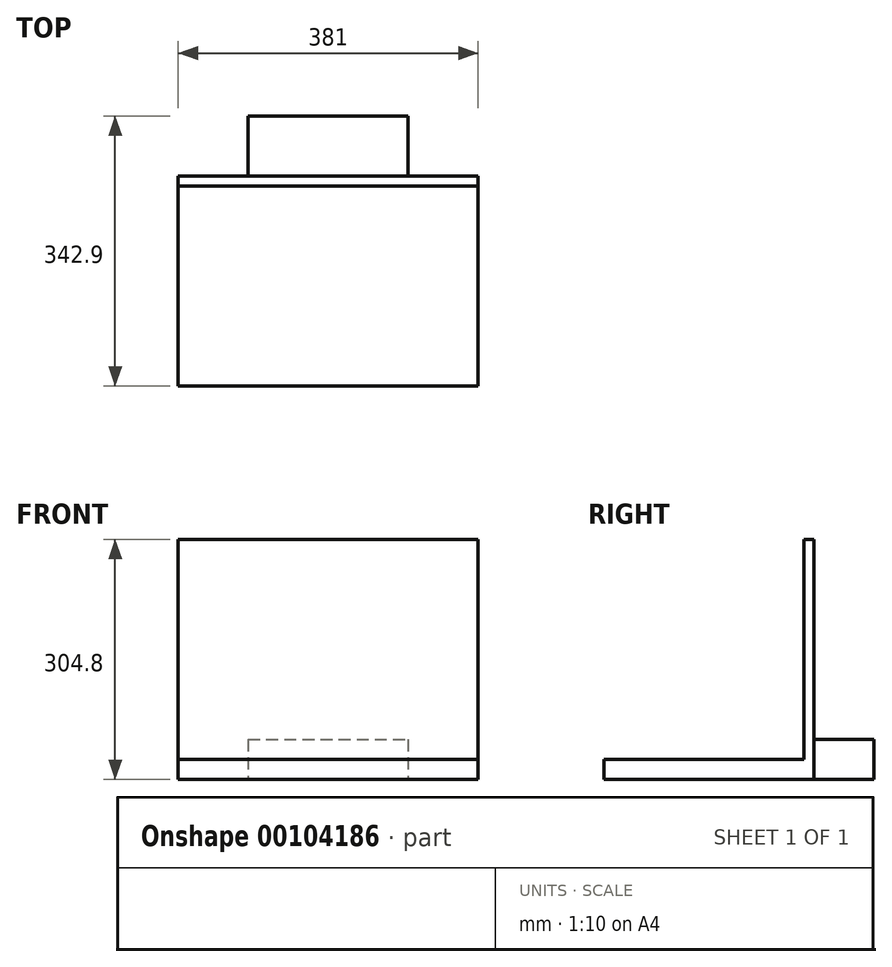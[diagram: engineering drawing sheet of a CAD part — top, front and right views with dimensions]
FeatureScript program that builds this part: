
annotation { "Feature Type Name" : "Feature", "Feature Type Description" : "" }
export const myFeature = defineFeature(function(context is Context, id is Id, definition is map)
    precondition{}
    {
        {
            var Q0;
            Q0=qCreatedBy(makeId("Top.planeOp"),FACE);
            var sketch = newSketch(context, id + "F0", { "sketchPlane" : qUnion([Q0])});
            skLineSegment(sketch, "E0.bottom", {"start": v(-208.4, -196.82) * mm, "end": v(172.6, -196.82) * mm});
            skLineSegment(sketch, "E0.top", {"start": v(-208.4, 57.18) * mm, "end": v(172.6, 57.18) * mm});
            skLineSegment(sketch, "E0.left", {"start": v(-208.4, -196.82) * mm, "end": v(-208.4, 57.18) * mm});
            skLineSegment(sketch, "E0.right", {"start": v(172.6, -196.82) * mm, "end": v(172.6, 57.18) * mm});
            skLineSegment(sketch, "E1.bottom", {"start": v(-119.5, 57.18) * mm, "end": v(83.7, 57.18) * mm});
            skSolve(sketch);
        }
        {
            var Q0;
            Q0 = qSketchRegion(id + "F0", true);
            extrude(context, id + "F1", {"entities" : qUnion([Q0]), "depth" : 25.4 * mm});
        }
        {
            var Q0;
            Q0=qCreatedBy(makeId("Top.planeOp"),FACE);
            var sketch = newSketch(context, id + "F2", { "sketchPlane" : qUnion([Q0])});
            skLineSegment(sketch, "E2.bottom", {"start": v(-208.4, 57.18) * mm, "end": v(172.6, 57.18) * mm});
            skLineSegment(sketch, "E2.top", {"start": v(-208.4, 69.88) * mm, "end": v(172.6, 69.88) * mm});
            skLineSegment(sketch, "E2.left", {"start": v(-208.4, 57.18) * mm, "end": v(-208.4, 69.88) * mm});
            skLineSegment(sketch, "E2.right", {"start": v(172.6, 57.18) * mm, "end": v(172.6, 69.88) * mm});
            skSolve(sketch);
        }
        {
            var Q0;
            Q0=qCreatedBy(makeId("Top.planeOp"),FACE);
            var sketch = newSketch(context, id + "F3", { "sketchPlane" : qUnion([Q0])});
            skLineSegment(sketch, "E3.bottom", {"start": v(-119.5, 146.08) * mm, "end": v(83.7, 146.08) * mm});
            skLineSegment(sketch, "E3.top", {"start": v(-119.5, 69.88) * mm, "end": v(83.7, 69.88) * mm});
            skLineSegment(sketch, "E3.left", {"start": v(-119.5, 146.08) * mm, "end": v(-119.5, 69.88) * mm});
            skLineSegment(sketch, "E3.right", {"start": v(83.7, 146.08) * mm, "end": v(83.7, 69.88) * mm});
            skSolve(sketch);
        }
        {
            var Q0;
            Q0 = qSketchRegion(id + "F2", true);
            extrude(context, id + "F4", {"entities" : qUnion([Q0]), "operationType" : NewBodyOperationType.ADD, "depth" : 304.8 * mm});
        }
        {
            var Q0;
            Q0 = qSketchRegion(id + "F3", true);
            extrude(context, id + "F5", {"entities" : qUnion([Q0]), "operationType" : NewBodyOperationType.ADD, "depth" : 50.8 * mm});
        }
    });
